# Revit family: OKA-W, Kanaleinheit, blind, Höhe 60-110mm
name_source: partatom
category: Generic Models
revit_build: Autodesk Revit 2015 (Build: 20140606_1530(x64)
units: mm (PartAtom-declared; Revit-internal decimal feet)

## types (5) — shared parameters
Manufacturer = OBO Bettermann
Material = Steel, Galvanized
URL = http://www.obo-bettermann.com

## per-type parameters (varying)
| type | Article Type | GTIN | Manufacturer Art. No. | Width |
| OKA-W2006050 | OKA-W2006050

OKA-W2006050
OKA-W2006050 | 4012195244196
4012195244196 | 7424420

7424420
7424420 | 200 mm  [stored 0.656168 ft] |
| OKA-W3006050 | OKA-W3006050 | 4012195244202

4012195244202

4012195244202

4012195244202

4012195244202

4012195244202

4012195244202
4012195244202 | 7424422

7424422

7424422

7424422
.
7424422
.
7424422
.
7424422
.
7424422
.
7424422
.
7424422

7424422
7424422 | 300 mm  [stored 0.984252 ft] |
| OKA-W4006050 | OKA-W4006050 | 4012195244233 | 7424424

7424424 | 400 mm  [stored 1.31234 ft] |
| OKA-W5006050 | OKA-W5006050 | 4012195244240 | 7424426

7424426

7424426

7424426
7424426 | 500 mm  [stored 1.64042 ft] |
| OKA-W6006050 | OKA-W6006050 | 4012195244257 | 7424428 | 600 mm |

note: [stored X ft] marks values corroborated as IEEE doubles in the binary element streams (Revit-internal decimal feet)

## geometry (parser evidence)
native form markers: Sweep x2
no freeform markers — native parametric forms only
